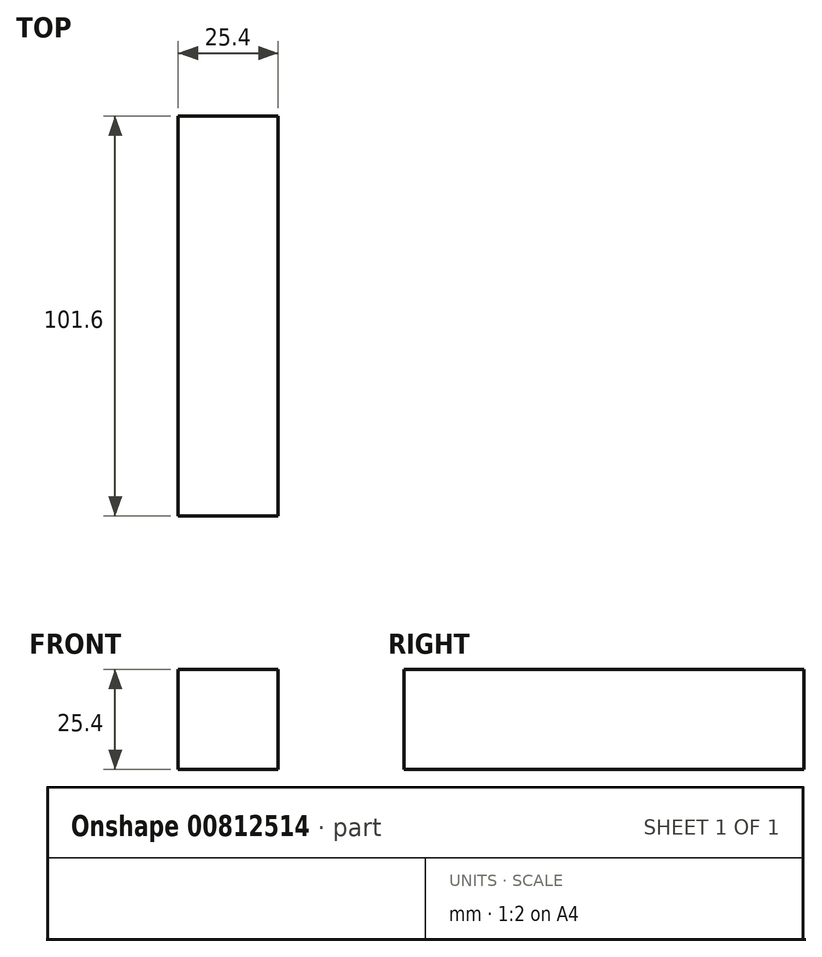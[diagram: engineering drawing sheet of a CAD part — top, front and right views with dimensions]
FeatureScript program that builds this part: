
annotation { "Feature Type Name" : "Feature", "Feature Type Description" : "" }
export const myFeature = defineFeature(function(context is Context, id is Id, definition is map)
    precondition{}
    {
        {
            var Q0;
            Q0=qCreatedBy(makeId("Front.planeOp"),FACE);
            var sketch = newSketch(context, id + "F0", { "sketchPlane" : qUnion([Q0])});
            skLineSegment(sketch, "E0.bottom", {"start": v(-12.7, 65.81) * mm, "end": v(12.7, 65.81) * mm});
            skLineSegment(sketch, "E0.top", {"start": v(-12.7, 40.41) * mm, "end": v(12.7, 40.41) * mm});
            skLineSegment(sketch, "E0.left", {"start": v(-12.7, 65.81) * mm, "end": v(-12.7, 40.41) * mm});
            skLineSegment(sketch, "E0.right", {"start": v(12.7, 65.81) * mm, "end": v(12.7, 40.41) * mm});
            skSolve(sketch);
        }
        {
            var Q0;
            Q0=makeQuery(id+"F0.imprint","IMPRINT",FACE,{"disambiguationData":[TD([[makeQuery(id+"F0.imprint","IMPRINT",EDGE,{"derivedFrom":sQuery(id+"F0.wireOp",EDGE,"E0.bottom")}),-1.0]])]});
            extrude(context, id + "F1", {"entities" : qUnion([Q0]), "endBound" : BoundingType.SYMMETRIC, "depth" : 101.6 * mm, "offsetDistance" : 25.4 * mm});
        }
    });
